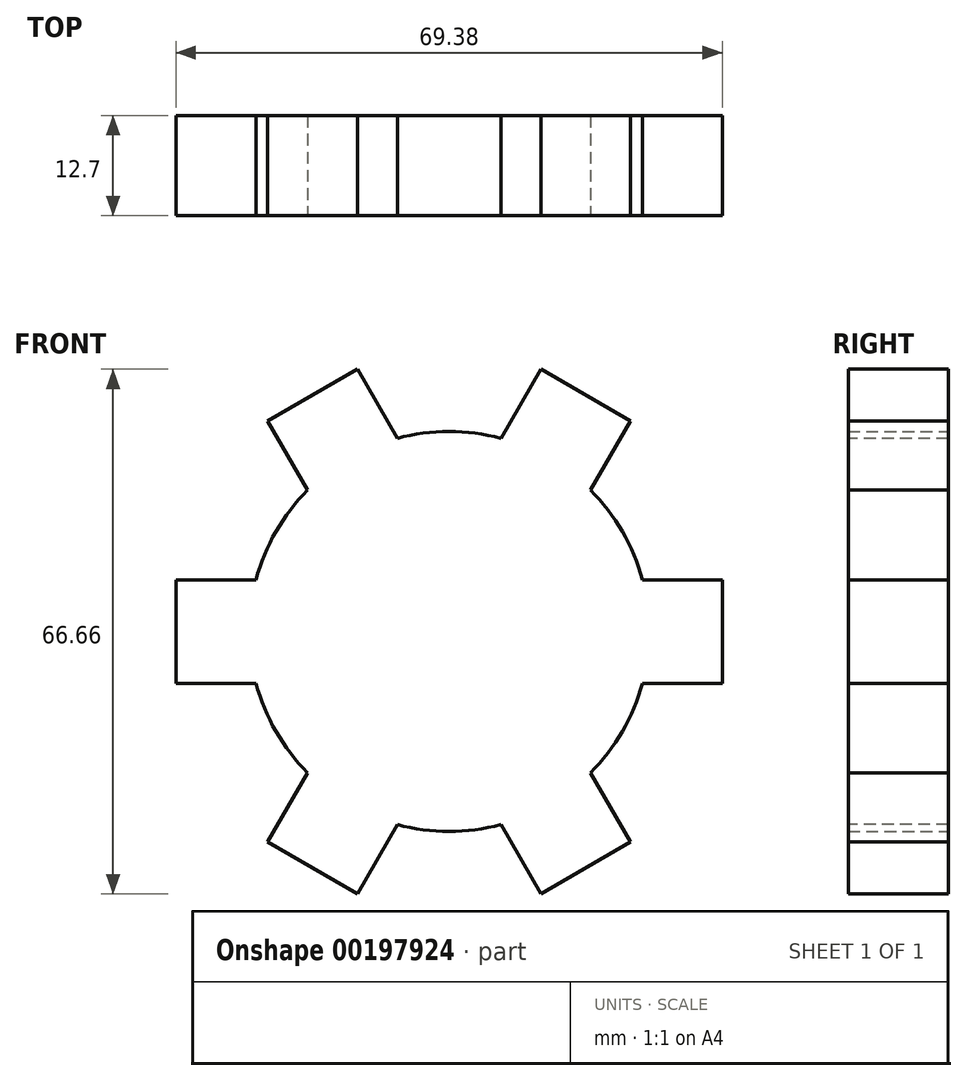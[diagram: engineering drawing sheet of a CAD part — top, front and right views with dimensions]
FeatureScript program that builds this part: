
annotation { "Feature Type Name" : "Feature", "Feature Type Description" : "" }
export const myFeature = defineFeature(function(context is Context, id is Id, definition is map)
    precondition{}
    {
        {
            var Q0;
            Q0=qCreatedBy(makeId("Front.planeOp"),FACE);
            var sketch = newSketch(context, id + "F0", { "sketchPlane" : qUnion([Q0])});
            skCircle(sketch, "E0", {"center": v(0, 0) * mm, "radius": 25.4 * mm});
            skSolve(sketch);
        }
        {
            var Q0;
            Q0=makeQuery(id+"F0.imprint","IMPRINT",FACE,{"disambiguationData":[TD([[makeQuery(id+"F0.imprint","IMPRINT",EDGE,{"derivedFrom":sQuery(id+"F0.wireOp",EDGE,"E0")}),1.0]])]});
            extrude(context, id + "F1", {"entities" : qUnion([Q0]), "endBound" : BoundingType.SYMMETRIC, "depth" : 12.7 * mm});
        }
        {
            var Q0;
            Q0=makeQuery(id+"F1.opExtrude","CAP_FACE",FACE,{"disambiguationData":[OSD([sQuery(id+"F0.wireOp",EDGE,"E0")])],"isStart":false});
            var sketch = newSketch(context, id + "F2", { "sketchPlane" : qUnion([Q0])});
            skLineSegment(sketch, "E1", {"start": v(0, 0) * mm, "end": v(25.4, 0) * mm});
            skLineSegment(sketch, "E2", {"start": v(25.4, 0) * mm, "end": v(0, 0) * mm});
            skLineSegment(sketch, "E3", {"start": v(0, 0) * mm, "end": v(24.53, 6.57) * mm});
            skLineSegment(sketch, "E4", {"start": v(0, 0) * mm, "end": v(24.53, -6.57) * mm});
            skLineSegment(sketch, "E5", {"start": v(24.53, 6.57) * mm, "end": v(24.53, -6.57) * mm});
            skLineSegment(sketch, "E6.0", {"start": v(34.7, 6.57) * mm, "end": v(34.7, -6.57) * mm});
            skLineSegment(sketch, "E7", {"start": v(34.7, 6.57) * mm, "end": v(24.53, 6.57) * mm});
            skLineSegment(sketch, "E8", {"start": v(34.7, -6.57) * mm, "end": v(24.53, -6.57) * mm});
            skSolve(sketch);
        }
        {
            var Q0;
            {var subQ0=sQuery(id+"F2.wireOp",EDGE,"E3");Q0=makeQuery(id+"F2.imprint","IMPRINT",FACE,{"disambiguationData":[TD([[makeQuery(id+"F2.imprint","IMPRINT",EDGE,{"derivedFrom":subQ0}),-1.0]])]});}
            var Q1;
            {var subQ0=sQuery(id+"F2.wireOp",EDGE,"E4");Q1=makeQuery(id+"F2.imprint","IMPRINT",FACE,{"disambiguationData":[TD([[makeQuery(id+"F2.imprint","IMPRINT",EDGE,{"derivedFrom":subQ0}),1.0]])]});}
            var Q2;
            {var subQ0=sQuery(id+"F2.wireOp",EDGE,"E2");var subQ1=makeQuery(id+"F1.opExtrude","CAP_EDGE",EDGE,{"disambiguationData":[OSD([sQuery(id+"F0.wireOp",EDGE,"E0")])],"isStart":false});var subQ2=makeQuery(id+"F2.imprint","INTERSECT",VERTEX,{"derivedFrom":[subQ1,subQ0]});Q2=makeQuery(id+"F2.imprint","IMPRINT",FACE,{"disambiguationData":[TD([[makeQuery(id+"F2.imprint","IMPRINT",EDGE,{"disambiguationData":[TD([[subQ2,-1.0]])],"derivedFrom":subQ0}),-1.0]])]});}
            var Q3;
            {var subQ0=sQuery(id+"F2.wireOp",EDGE,"E2");var subQ1=makeQuery(id+"F1.opExtrude","CAP_EDGE",EDGE,{"disambiguationData":[OSD([sQuery(id+"F0.wireOp",EDGE,"E0")])],"isStart":false});var subQ2=makeQuery(id+"F2.imprint","INTERSECT",VERTEX,{"derivedFrom":[subQ1,subQ0]});Q3=makeQuery(id+"F2.imprint","IMPRINT",FACE,{"disambiguationData":[TD([[makeQuery(id+"F2.imprint","IMPRINT",EDGE,{"disambiguationData":[TD([[subQ2,-1.0]])],"derivedFrom":subQ0}),1.0]])]});}
            var Q4;
            Q4=makeQuery(id+"F2.imprint","IMPRINT",FACE,{"disambiguationData":[TD([[makeQuery(id+"F2.imprint","IMPRINT",EDGE,{"derivedFrom":sQuery(id+"F2.wireOp",EDGE,"E6.0")}),-1.0]])]});
            extrude(context, id + "F3", {"entities" : qUnion([Q0, Q1, Q2, Q3, Q4]), "operationType" : NewBodyOperationType.ADD, "oppositeDirection" : true, "depth" : 12.7 * mm});
        }
        {
            var Q0;
            Q0=qCreatedBy(makeId("Right.planeOp"),FACE);
            var sketch = newSketch(context, id + "F4", { "sketchPlane" : qUnion([Q0])});
            skLineSegment(sketch, "E9", {"start": v(0, 0) * mm, "end": v(-29.6, 0) * mm});
            skSolve(sketch);
        }
        {
            var Q0;
            Q0=makeQuery(id+"F1.opExtrude","SWEPT_BODY",BODY,{"disambiguationData":[OSD([sQuery(id+"F0.wireOp",EDGE,"E0")])]});
            var Q1;
            Q1=sQuery(id+"F4.wireOp",EDGE,"E9");
            circularPattern(context, id + "F5", {"operationType" : NewBodyOperationType.ADD, "entities" : qUnion([Q0]), "axis" : qUnion([Q1]), "angle" : 360 * degree, "instanceCount" : 6, "oppositeDirection" : true, "equalSpace" : true});
        }
    });
